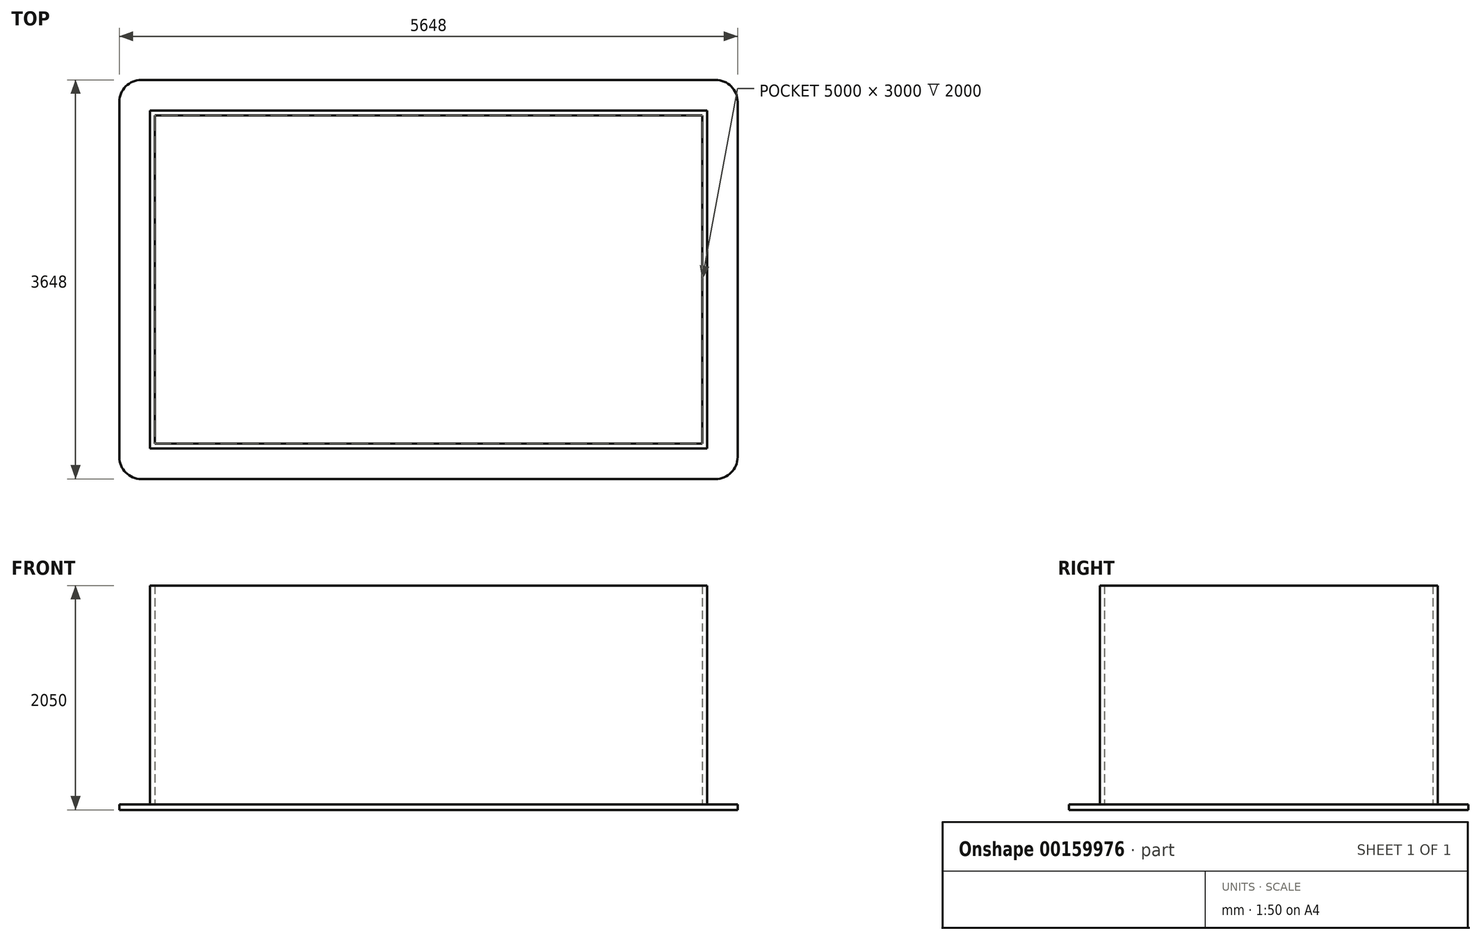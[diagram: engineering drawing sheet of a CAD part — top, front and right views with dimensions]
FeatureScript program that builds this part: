
annotation { "Feature Type Name" : "Feature", "Feature Type Description" : "" }
export const myFeature = defineFeature(function(context is Context, id is Id, definition is map)
    precondition{}
    {
        {
            var Q0;
            Q0=qCreatedBy(makeId("Top.planeOp"),FACE);
            var sketch = newSketch(context, id + "F0", { "sketchPlane" : qUnion([Q0])});
            skLineSegment(sketch, "E0.bottom", {"start": v(-2500, 1500) * mm, "end": v(2500, 1500) * mm, "construction": true});
            skLineSegment(sketch, "E0.top", {"start": v(-2500, -1500) * mm, "end": v(2500, -1500) * mm, "construction": true});
            skLineSegment(sketch, "E0.left", {"start": v(-2500, 1500) * mm, "end": v(-2500, -1500) * mm, "construction": true});
            skLineSegment(sketch, "E0.right", {"start": v(2500, 1500) * mm, "end": v(2500, -1500) * mm, "construction": true});
            skPoint(sketch, "E0.middle", {"position": v(0, 0) * mm});
            skLineSegment(sketch, "E1", {"start": v(-2500, 1500) * mm, "end": v(-2544, 1544) * mm});
            skLineSegment(sketch, "E2", {"start": v(-2544, 1544) * mm, "end": v(-2544, -1544) * mm});
            skLineSegment(sketch, "E3", {"start": v(-2544, -1544) * mm, "end": v(-2500, -1500) * mm});
            skLineSegment(sketch, "E4", {"start": v(0, 1735.84) * mm, "end": v(0, -1849.91) * mm, "construction": true});
            skPoint(sketch, "E4.endSnap0", {"position": v(0, -1500) * mm});
            skLineSegment(sketch, "E5", {"start": v(-2544, 1544) * mm, "end": v(0, 1544) * mm});
            skLineSegment(sketch, "E6", {"start": v(0, 1544) * mm, "end": v(0, 1500) * mm});
            skLineSegment(sketch, "E7", {"start": v(0, 1500) * mm, "end": v(-2500, 1500) * mm});
            skLineSegment(sketch, "E8", {"start": v(-2544, -1544) * mm, "end": v(0, -1544) * mm});
            skLineSegment(sketch, "E9", {"start": v(0, -1544) * mm, "end": v(0, -1500) * mm});
            skLineSegment(sketch, "E10", {"start": v(-2500, -1500) * mm, "end": v(0, -1500) * mm});
            skLineSegment(sketch, "E11", {"start": v(-2500, -1500) * mm, "end": v(-2500, 1500) * mm});
            skSolve(sketch);
        }
        {
            var Q0;
            Q0=makeQuery(id+"F0.imprint","IMPRINT",FACE,{"disambiguationData":[TD([[makeQuery(id+"F0.imprint","IMPRINT",EDGE,{"derivedFrom":sQuery(id+"F0.wireOp",EDGE,"E1")}),1.0]])]});
            var Q1;
            Q1=makeQuery(id+"F0.imprint","IMPRINT",FACE,{"disambiguationData":[TD([[makeQuery(id+"F0.imprint","IMPRINT",EDGE,{"derivedFrom":sQuery(id+"F0.wireOp",EDGE,"E1")}),-1.0]])]});
            var Q2;
            Q2=makeQuery(id+"F0.imprint","IMPRINT",FACE,{"disambiguationData":[TD([[makeQuery(id+"F0.imprint","IMPRINT",EDGE,{"derivedFrom":sQuery(id+"F0.wireOp",EDGE,"E3")}),-1.0]])]});
            extrude(context, id + "F1", {"entities" : qUnion([Q0, Q1, Q2]), "depth" : 2000 * mm});
        }
        {
            var Q0;
            Q0=makeQuery(id+"F1.opExtrude","CAP_FACE",FACE,{"disambiguationData":[OSD([sQuery(id+"F0.wireOp",EDGE,"E2"),sQuery(id+"F0.wireOp",EDGE,"E5"),sQuery(id+"F0.wireOp",EDGE,"E6"),sQuery(id+"F0.wireOp",EDGE,"E7"),sQuery(id+"F0.wireOp",EDGE,"E8"),sQuery(id+"F0.wireOp",EDGE,"E9"),sQuery(id+"F0.wireOp",EDGE,"E10"),sQuery(id+"F0.wireOp",EDGE,"E11")])],"isStart":true});
            var sketch = newSketch(context, id + "F2", { "sketchPlane" : qUnion([Q0])});
            skLineSegment(sketch, "E12.0", {"start": v(-2824, 1824) * mm, "end": v(0, 1824) * mm});
            skLineSegment(sketch, "E12.1", {"start": v(-2824, -1824) * mm, "end": v(-2824, 1824) * mm});
            skLineSegment(sketch, "E12.2", {"start": v(-2824, -1824) * mm, "end": v(0, -1824) * mm});
            skLineSegment(sketch, "E13", {"start": v(0, 1824) * mm, "end": v(0, -1824) * mm});
            skSolve(sketch);
        }
        {
            var Q0;
            {var subQ2=sQuery(id+"F2.wireOp",EDGE,"E12.0");Q0=makeQuery(id+"F2.imprint","IMPRINT",FACE,{"disambiguationData":[TD([[makeQuery(id+"F2.imprint","IMPRINT",EDGE,{"derivedFrom":subQ2}),-1.0]])]});}
            var Q1;
            {var subQ1=makeQuery(id+"F1.opExtrude","CAP_EDGE",EDGE,{"disambiguationData":[OSD([sQuery(id+"F0.wireOp",EDGE,"E7")])],"isStart":true});Q1=makeQuery(id+"F2.imprint","IMPRINT",FACE,{"disambiguationData":[TD([[makeQuery(id+"F2.imprint","IMPRINT",EDGE,{"derivedFrom":subQ1}),-1.0]])]});}
            var Q2;
            Q2=makeQuery(id+"F2.imprint","IMPRINT",FACE,{"disambiguationData":[TD([[makeQuery(id+"F2.imprint","IMPRINT",EDGE,{"derivedFrom":makeQuery(id+"F1.opExtrude","CAP_EDGE",EDGE,{"disambiguationData":[OSD([sQuery(id+"F0.wireOp",EDGE,"E2")])],"isStart":true})}),-1.0]])]});
            extrude(context, id + "F3", {"entities" : qUnion([Q0, Q1, Q2]), "operationType" : NewBodyOperationType.ADD, "depth" : 50 * mm});
        }
        {
            var Q0;
            Q0=makeQuery(id+"F3.opExtrude","SWEPT_EDGE",EDGE,{"disambiguationData":[OSD([sQuery(id+"F2.wireOp",EDGE,"E12.0"),sQuery(id+"F2.wireOp",EDGE,"E12.1")])]});
            var Q1;
            Q1=makeQuery(id+"F3.opExtrude","SWEPT_EDGE",EDGE,{"disambiguationData":[OSD([sQuery(id+"F2.wireOp",EDGE,"E12.1"),sQuery(id+"F2.wireOp",EDGE,"E12.2")])]});
            fillet(context, id + "F4", {"entities" : qUnion([Q0, Q1]), "radius" : 200 * mm, "tangentPropagation" : true, "allowEdgeOverflow" : false});
        }
        {
            var Q0;
            Q0=makeQuery(id+"F1.opExtrude","SWEPT_BODY",BODY,{"disambiguationData":[OSD([sQuery(id+"F0.wireOp",EDGE,"E2"),sQuery(id+"F0.wireOp",EDGE,"E5"),sQuery(id+"F0.wireOp",EDGE,"E6"),sQuery(id+"F0.wireOp",EDGE,"E7"),sQuery(id+"F0.wireOp",EDGE,"E8"),sQuery(id+"F0.wireOp",EDGE,"E9"),sQuery(id+"F0.wireOp",EDGE,"E10"),sQuery(id+"F0.wireOp",EDGE,"E11")])]});
            var Q1;
            Q1=makeQuery(id+"F3.boolean.opBoolean","MERGE",FACE,{"derivedFrom":[makeQuery(id+"F1.opExtrude","SWEPT_FACE",FACE,{"disambiguationData":[OSD([sQuery(id+"F0.wireOp",EDGE,"E6")])]}),makeQuery(id+"F1.opExtrude","SWEPT_FACE",FACE,{"disambiguationData":[OSD([sQuery(id+"F0.wireOp",EDGE,"E9")])]}),makeQuery(id+"F3.opExtrude","SWEPT_FACE",FACE,{"disambiguationData":[OSD([sQuery(id+"F2.wireOp",EDGE,"E13")])]})]});
            mirror(context, id + "F5", {"operationType" : NewBodyOperationType.ADD, "entities" : qUnion([Q0]), "mirrorPlane" : qUnion([Q1])});
        }
    });
